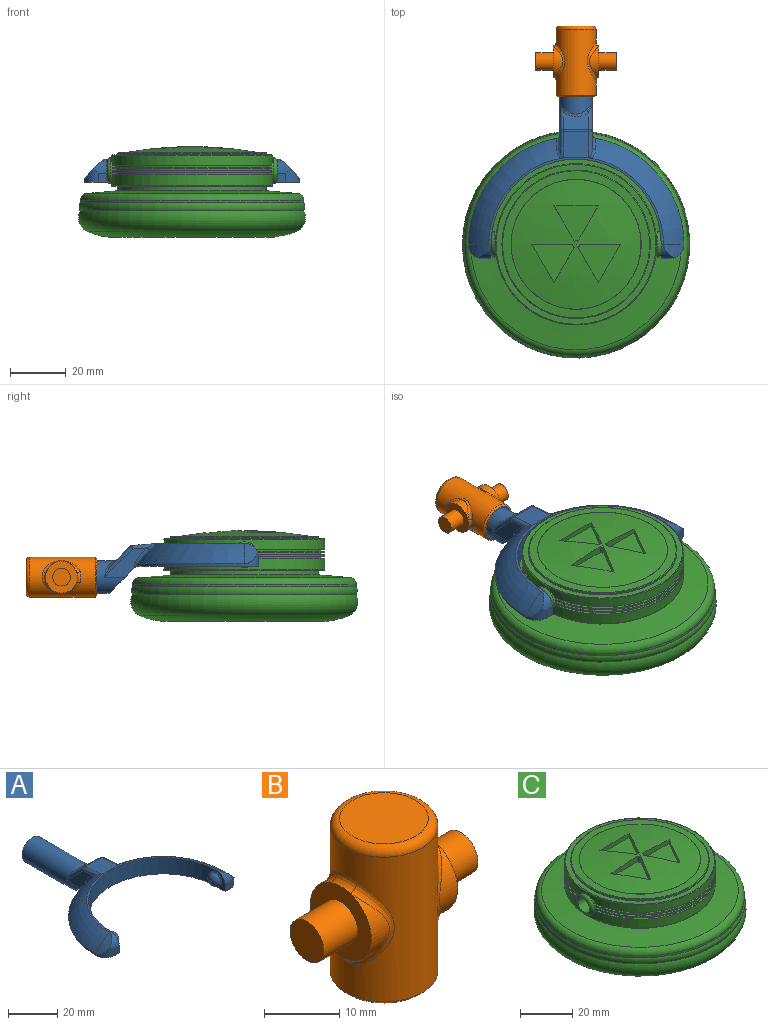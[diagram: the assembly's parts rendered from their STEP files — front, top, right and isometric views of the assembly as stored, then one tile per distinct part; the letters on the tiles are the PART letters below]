
ASSEMBLY  parts=3 mates=2
PART A: 48 faces, bbox 77.3x80.8x18.2 mm
  f0: plane 11.99x9.83mm, normal (0,-0.71,-0.71), area 141.5mm2, adj f1,f2,f9,f30,f43,f46
  f1: plane 15.39x10.49mm, normal (-1,0,0), area 63.5mm2, adj f0,f30,f32,f36,f46,f47
  f2: plane 15.39x10.49mm, normal (1,0,0), area 63.5mm2, adj f0,f30,f34,f39,f43,f44
  f3: plane 9.14x6.37mm, normal (0,0.71,0.71), area 67.6mm2, adj f35,f36,f39,f40
  f4: cylinder r=38.61mm len=37.99mm, axis (0,0,-1), area 42.6mm2, adj f6,f9,f17,f46,f47
  f5: torus R=19.3mm, axis (0,0,-1), area 507.8mm2, adj f10,f11,f12,f29,f42,f44
  f6: torus R=19.3mm, axis (0,0,-1), area 507.8mm2, adj f4,f11,f15,f28,f45,f47
  f7: cylinder r=30.48mm len=60.96mm, axis (0,0,-1), area 746.6mm2, adj f8,f9,f11,f14,f21,f24
  f8: plane 8.13x5.08mm, normal (-1,0,0), area 19.9mm2, adj f7,f9,f13,f19,f24
  f9: plane 77.22x43.73mm, normal (0,0,-1), area 956.2mm2, adj f0,f4,f7,f8,f10,f13,f14,f16
  f10: cylinder r=38.61mm len=37.99mm, axis (0,0,-1), area 42.6mm2, adj f5,f9,f20,f43,f44
  f11: plane 62.55x30.95mm, normal (0,0,1), area 75mm2, adj f5,f6,f7,f18,f19,f27
  f12: cylinder r=22.71mm len=7.33mm, axis (0,1,0), area 24.8mm2, adj f5,f19,f20
  f13: plane 3.05x3.05mm, normal (0,-1,0), area 9.3mm2, adj f8,f9,f19,f20
  f14: plane 8.13x5.08mm, normal (1,0,0), area 19.9mm2, adj f7,f9,f16,f18,f21
  f15: cylinder r=22.71mm len=7.33mm, axis (0,1,0), area 24.8mm2, adj f6,f17,f18
  f16: plane 3.05x3.05mm, normal (0,-1,0), area 9.3mm2, adj f9,f14,f17,f18
  f17: cylinder r=5.08mm len=5.08mm, axis (0,0,-1), area 21.9mm2, adj f4,f9,f15,f16,f18
  f18: cylinder r=5.08mm len=5.08mm, axis (-1,0,0), area 21.9mm2, adj f11,f14,f15,f16,f17
  f19: cylinder r=5.08mm len=5.08mm, axis (-1,0,0), area 21.9mm2, adj f8,f11,f12,f13,f20
  f20: cylinder r=5.08mm len=5.08mm, axis (0,0,-1), area 21.9mm2, adj f9,f10,f12,f13,f19
  f21: cylinder r=3.17mm len=6.35mm, axis (-1,0,0), area 12.7mm2, adj f7,f14,f23
  f22: plane 1.27x1.27mm, normal (1,0,0), area 1.3mm2, adj f23
  f23: torus R=0.64mm, axis (1,0,0), area 56.5mm2, adj f21,f22
  f24: cylinder r=3.17mm len=6.35mm, axis (1,0,0), area 12.7mm2, adj f7,f8,f26
  f25: plane 1.27x1.27mm, normal (-1,0,0), area 1.3mm2, adj f26
  f26: torus R=0.64mm, axis (-1,0,0), area 56.5mm2, adj f24,f25
  f27: plane 9.86x9.36mm, normal (0,0.09,1), area 85.6mm2, adj f11,f28,f29,f32,f34,f35,f42,f45
  f28: plane 1.04x0.17mm, normal (0,-1,0), area 0mm2, adj f6,f27,f45
  f29: plane 1.04x0.17mm, normal (0,-1,0), area 0mm2, adj f5,f27,f42
  f30: cylinder r=5.84mm len=33.01mm, axis (0,-1,0), area 1029.7mm2, adj f0,f1,f2,f31,f38,f40,f41
  f31: plane 11.68x11.68mm, normal (0,1,0), area 107.2mm2, adj f30
  f32: cylinder r=1.27mm len=9.13mm, axis (0,-1,0.09), area 14.4mm2, adj f1,f27,f33,f45
  f33: sphere r=1.27mm, area 1.5mm2, adj f32,f35,f36
  f34: cylinder r=1.27mm len=9.13mm, axis (0,1,-0.09), area 14.4mm2, adj f2,f27,f37,f42
  f35: cylinder r=1.27mm len=9.14mm, axis (-1,0,0), area 8.1mm2, adj f3,f27,f33,f37
  f36: cylinder r=1.27mm len=10.91mm, axis (0,-0.71,0.71), area 23.1mm2, adj f1,f3,f33,f38
  f37: sphere r=1.27mm, area 1.5mm2, adj f34,f35,f39
  f38: bspline ~4.55x2.75mm, area 2.3mm2, adj f30,f36,f40
  f39: cylinder r=1.27mm len=10.91mm, axis (0,0.71,-0.71), area 23.1mm2, adj f2,f3,f37,f41
  f40: bspline ~9.14x2.56mm, area 10.7mm2, adj f3,f30,f38,f41
  f41: bspline ~5.23x3.53mm, area 2.3mm2, adj f30,f39,f40
  f42: bspline ~4.62x3.14mm, area 5.2mm2, adj f5,f27,f29,f34,f44
  f43: cylinder r=1.27mm len=1.74mm, axis (0,0,-1), area 1.9mm2, adj f0,f2,f9,f10,f44
  f44: bspline ~8.6x7.86mm, area 11.9mm2, adj f2,f5,f10,f42,f43
  f45: bspline ~4.62x3.14mm, area 5.2mm2, adj f6,f27,f28,f32,f47
  f46: cylinder r=1.27mm len=1.74mm, axis (0,0,-1), area 1.9mm2, adj f0,f1,f4,f9,f47
  f47: bspline ~8.6x7.86mm, area 11.9mm2, adj f1,f4,f6,f45,f46
PART B: 25 faces, bbox 28.9x15.5x25.4 mm
  f0: cylinder r=5.71mm len=10.81mm, axis (-1,0,0), area 26.2mm2, adj f5,f15
  f1: cylinder r=5.71mm len=10.81mm, axis (-1,0,0), area 26.2mm2, adj f8,f11
  f2: cylinder r=7.14mm len=23.5mm, axis (0,0,-1), area 763.2mm2, adj f9,f10,f11,f12,f13,f14,f15,f16
  f3: plane 11.75x11.75mm, normal (0,0,1), area 108.4mm2, adj f17
  f4: plane 13.02x13.02mm, normal (0,0,-1), area 16.3mm2, adj f22,f24
  f5: plane 11.46x11.46mm, normal (1,0,0), area 70.9mm2, adj f0,f6,f13,f16,f18
  f6: cylinder r=5.71mm len=10.81mm, axis (-1,0,0), area 26.2mm2, adj f5,f14
  f7: cylinder r=5.71mm len=10.81mm, axis (-1,0,0), area 26.2mm2, adj f8,f10
  f8: plane 11.46x11.46mm, normal (-1,0,0), area 70.9mm2, adj f1,f7,f9,f12,f20
  f9: bspline ~4.64x1.73mm, area 6.5mm2, adj f2,f8,f10,f11
  f10: bspline ~13.62x4.91mm, area 20.7mm2, adj f2,f7,f9,f12
  f11: bspline ~13.6x4.87mm, area 20.7mm2, adj f1,f2,f9,f12
  f12: bspline ~4.64x1.73mm, area 6.5mm2, adj f2,f8,f10,f11
  f13: bspline ~4.64x1.73mm, area 6.5mm2, adj f2,f5,f14,f15
  f14: bspline ~13.62x4.91mm, area 20.7mm2, adj f2,f6,f13,f16
  f15: bspline ~13.6x4.87mm, area 20.7mm2, adj f0,f2,f13,f16
  f16: bspline ~4.64x1.73mm, area 6.5mm2, adj f2,f5,f14,f15
  f17: torus R=5.87mm, axis (0,0,1), area 83.8mm2, adj f2,f3
  f18: cylinder r=3.17mm len=6.35mm, axis (-1,0,0), area 126.7mm2, adj f5,f19
  f19: plane 6.35x6.35mm, normal (1,0,0), area 31.7mm2, adj f18
  f20: cylinder r=3.17mm len=6.35mm, axis (1,0,0), area 126.7mm2, adj f8,f21
  f21: plane 6.35x6.35mm, normal (-1,0,0), area 31.7mm2, adj f20
  f22: cylinder r=6.1mm len=22.86mm, axis (0,0,-1), area 875.6mm2, adj f4,f23
  f23: plane 12.19x12.19mm, normal (0,0,-1), area 116.7mm2, adj f22
  f24: cone r=7.14mm half-angle=45deg, axis (0,0,1), area 38.5mm2, adj f2,f4
PART C: 64 faces, bbox 96.2x96.2x32.5 mm
  f0: cylinder r=28.87mm len=57.73mm, axis (0,0,-1), area 699.9mm2, adj f5,f6,f54,f55,f60
  f1: plane 57.02x24.34mm, normal (0,0,-1), area 101.1mm2, adj f4,f8,f54,f55
  f2: plane 57.02x24.34mm, normal (0,0,-1), area 101.1mm2, adj f3,f7,f54,f55
  f3: cylinder r=27.6mm len=54.49mm, axis (0,0,-1), area 49.4mm2, adj f2,f6,f54,f55
  f4: cylinder r=27.6mm len=54.49mm, axis (0,0,-1), area 49.4mm2, adj f1,f5,f54,f55
  f5: plane 57.06x24.48mm, normal (0,0,1), area 101.4mm2, adj f0,f4,f54,f55
  f6: plane 57.06x24.48mm, normal (0,0,1), area 101.4mm2, adj f0,f3,f54,f55
  f7: cylinder r=28.87mm len=57.02mm, axis (0,0,-1), area 51.8mm2, adj f2,f14,f54,f55
  f8: cylinder r=28.87mm len=57.02mm, axis (0,0,-1), area 51.8mm2, adj f1,f13,f54,f55
  f9: plane 57.02x24.34mm, normal (0,0,-1), area 101.1mm2, adj f12,f16,f54,f55
  f10: plane 57.02x24.34mm, normal (0,0,-1), area 101.1mm2, adj f11,f15,f54,f55
  f11: cylinder r=27.6mm len=54.45mm, axis (0,0,-1), area 49.2mm2, adj f10,f14,f54,f55
  f12: cylinder r=27.6mm len=54.45mm, axis (0,0,-1), area 49.2mm2, adj f9,f13,f54,f55
  f13: plane 57.01x24.3mm, normal (0,0,1), area 101mm2, adj f8,f12,f54,f55
  f14: plane 57.01x24.3mm, normal (0,0,1), area 101mm2, adj f7,f11,f54,f55
  f15: cylinder r=28.87mm len=57.06mm, axis (0,0,-1), area 51.9mm2, adj f10,f22,f54,f55
  f16: cylinder r=28.87mm len=57.06mm, axis (0,0,-1), area 51.9mm2, adj f9,f21,f54,f55
  f17: plane 57.13x24.71mm, normal (0,0,-1), area 102mm2, adj f20,f23,f54,f55
  f18: plane 57.13x24.71mm, normal (0,0,-1), area 102mm2, adj f19,f23,f54,f55
  f19: cylinder r=27.6mm len=54.56mm, axis (0,0,-1), area 49.6mm2, adj f18,f22,f54,f55
  f20: cylinder r=27.6mm len=54.56mm, axis (0,0,-1), area 49.6mm2, adj f17,f21,f54,f55
  f21: plane 57.06x24.48mm, normal (0,0,1), area 101.4mm2, adj f16,f20,f54,f55
  f22: plane 57.06x24.48mm, normal (0,0,1), area 101.4mm2, adj f15,f19,f54,f55
  f23: cylinder r=28.87mm len=57.73mm, axis (0,0,-1), area 595.9mm2, adj f17,f18,f54,f55,f61
  f24: sphere r=135.39mm, area 1385.3mm2, adj f38,f39,f40,f41,f43,f44,f45,f46
  f25: plane 39.33x39.33mm, normal (0,0,-1), area 1214.6mm2, adj f26
  f26: torus R=20.12mm, axis (0,0,-1), area 1429.3mm2, adj f25,f27
  f27: torus R=27.74mm, axis (0,0,-1), area 3542.1mm2, adj f26,f28
  f28: torus R=35.36mm, axis (0,0,-1), area 2180.1mm2, adj f27,f29
  f29: torus R=37.35mm, axis (0,0,-1), area 734.6mm2, adj f28,f30
  f30: cylinder r=40.06mm len=80.11mm, axis (0,0,-1), area 213.3mm2, adj f29,f34
  f31: cone r=26.57mm half-angle=85deg, axis (0,0,-1), area 2265mm2, adj f32,f34
  f32: cylinder r=26.57mm len=53.14mm, axis (0,0,-1), area 265mm2, adj f31,f33
  f33: plane 57.23x57.23mm, normal (0,0,-1), area 354.5mm2, adj f32,f60
  f34: torus R=37.52mm, axis (0,0,1), area 928.6mm2, adj f30,f31
  f35: cone r=26.57mm half-angle=87deg, axis (0,0,-1), area 475.4mm2, adj f62,f63
  f36: cylinder r=26.57mm len=53.14mm, axis (0,0,-1), area 92.3mm2, adj f37,f62
  f37: plane 57.23x57.23mm, normal (0,0,1), area 354.5mm2, adj f36,f61
  f38: cylinder r=1.27mm len=2.53mm, axis (0,0,1), area 3.4mm2, adj f24,f39,f41,f42
  f39: plane 14.61x2.53mm, normal (0,-1,0), area 32.2mm2, adj f24,f38,f40,f42
  f40: plane 13.75x7.94mm, normal (0.87,0.5,0), area 28mm2, adj f24,f39,f41,f42
  f41: plane 12.65x7.3mm, normal (-0.87,0.5,0), area 32.2mm2, adj f24,f38,f40,f42
  f42: plane 15.24x13.75mm, normal (0,0,1), area 108.3mm2, adj f38,f39,f40,f41
  f43: cylinder r=1.27mm len=2.53mm, axis (0,0,1), area 3.4mm2, adj f24,f44,f46,f47
  f44: plane 12.65x7.3mm, normal (0.87,0.5,0), area 32.2mm2, adj f24,f43,f45,f47
  f45: plane 13.75x7.94mm, normal (-0.87,0.5,0), area 28mm2, adj f24,f44,f46,f47
  f46: plane 14.61x2.53mm, normal (0,-1,0), area 32.2mm2, adj f24,f43,f45,f47
  f47: plane 15.24x13.75mm, normal (0,0,1), area 108.3mm2, adj f43,f44,f45,f46
  f48: cylinder r=1.27mm len=2.53mm, axis (0,0,1), area 3.4mm2, adj f24,f49,f51,f52
  f49: plane 12.65x7.3mm, normal (-0.87,0.5,0), area 32.2mm2, adj f24,f48,f50,f52
  f50: plane 15.88x1.84mm, normal (0,-1,0), area 28mm2, adj f24,f49,f51,f52
  f51: plane 12.65x7.3mm, normal (0.87,0.5,0), area 32.2mm2, adj f24,f48,f50,f52
  f52: plane 15.88x12.65mm, normal (0,0,1), area 108.3mm2, adj f48,f49,f50,f51
  f53: plane 6.6x6.6mm, normal (1,0,0), area 2.6mm2, adj f58,f59
  f54: cylinder r=4.57mm len=9.14mm, axis (-1,0,0), area 20.1mm2, adj f0,f1,f2,f3,f4,f5,f6,f7
  f55: cylinder r=4.57mm len=9.14mm, axis (-1,0,0), area 20.1mm2, adj f0,f1,f2,f3,f4,f5,f6,f7
  f56: plane 6.6x6.6mm, normal (-1,0,0), area 2.6mm2, adj f57,f59
  f57: torus R=3.3mm, axis (1,0,0), area 51.5mm2, adj f55,f56
  f58: torus R=3.3mm, axis (1,0,0), area 51.5mm2, adj f53,f54
  f59: cylinder r=3.17mm len=60.96mm, axis (1,0,0), area 1216.1mm2, adj f53,f56
  f60: torus R=28.61mm, axis (0,0,1), area 72.1mm2, adj f0,f33
  f61: torus R=28.61mm, axis (0,0,-1), area 72.1mm2, adj f23,f37
  f62: torus R=26.31mm, axis (0,0,1), area 64.2mm2, adj f35,f36
  f63: torus R=23.29mm, axis (0,0,1), area 4.5mm2, adj f24,f35
PLACE A t=(32.34,27.52,20.85)mm
PLACE B rot(axis=(-1,0,0),90deg) t=(32.34,80.3,16.88)mm
PLACE C t=(32.34,27.52,33.52)mm
MATE revolute A.f24 <-> C.f54  axis (-1,0,0) through (62.82,27.52,24.92)mm
MATE revolute B.f2 <-> A.f30  axis (0,-1,0) through (32.34,103.16,16.88)mm
